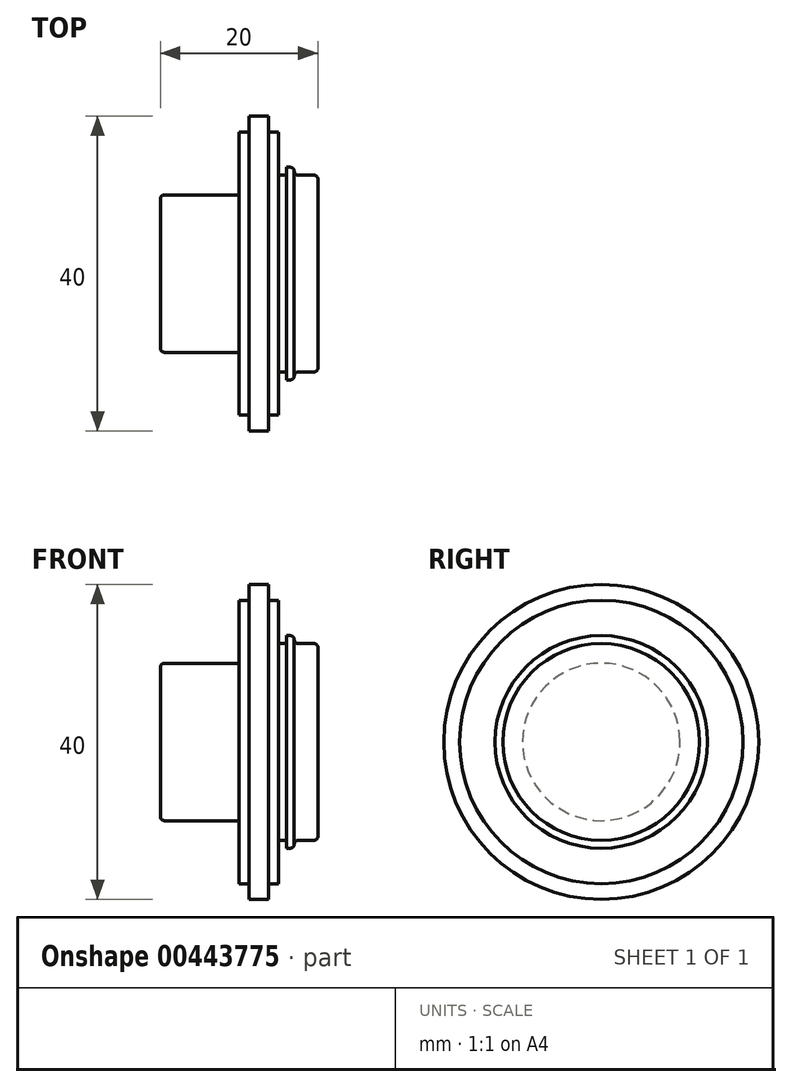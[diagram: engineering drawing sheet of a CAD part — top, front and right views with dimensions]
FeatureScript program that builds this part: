
annotation { "Feature Type Name" : "Feature", "Feature Type Description" : "" }
export const myFeature = defineFeature(function(context is Context, id is Id, definition is map)
    precondition{}
    {
        {
            var Q0;
            Q0=qCreatedBy(makeId("Front.planeOp"),FACE);
            var sketch = newSketch(context, id + "F0", { "sketchPlane" : qUnion([Q0])});
            skLineSegment(sketch, "E0", {"start": v(0, 0) * mm, "end": v(-20, 0) * mm});
            skLineSegment(sketch, "E1", {"start": v(-20, 0) * mm, "end": v(-20, 10) * mm});
            skLineSegment(sketch, "E2", {"start": v(-20, 10) * mm, "end": v(-10, 10) * mm});
            skLineSegment(sketch, "E3", {"start": v(-10, 10) * mm, "end": v(-10, 18) * mm});
            skLineSegment(sketch, "E4", {"start": v(-10, 18) * mm, "end": v(-8.75, 18) * mm});
            skLineSegment(sketch, "E5", {"start": v(-8.75, 18) * mm, "end": v(-8.75, 20) * mm});
            skLineSegment(sketch, "E6", {"start": v(-8.75, 20) * mm, "end": v(-6.25, 20) * mm});
            skLineSegment(sketch, "E7", {"start": v(-6.25, 20) * mm, "end": v(-6.25, 18) * mm});
            skLineSegment(sketch, "E8", {"start": v(-6.25, 18) * mm, "end": v(-5, 18) * mm});
            skLineSegment(sketch, "E9", {"start": v(-5, 18) * mm, "end": v(-5, 12.5) * mm});
            skLineSegment(sketch, "E10", {"start": v(-5, 12.5) * mm, "end": v(-4, 12.5) * mm});
            skLineSegment(sketch, "E11", {"start": v(-4, 12.5) * mm, "end": v(-4, 13.5) * mm});
            skLineSegment(sketch, "E12", {"start": v(-4, 13.5) * mm, "end": v(-3, 13.5) * mm});
            skLineSegment(sketch, "E13", {"start": v(-3, 13.5) * mm, "end": v(-3, 12.5) * mm});
            skLineSegment(sketch, "E14", {"start": v(-3, 12.5) * mm, "end": v(0, 12.5) * mm});
            skLineSegment(sketch, "E15", {"start": v(0, 12.5) * mm, "end": v(0, 0) * mm});
            skSolve(sketch);
        }
        {
            var Q0;
            Q0 = qSketchRegion(id + "F0", true);
            var Q1;
            Q1=sQuery(id+"F0.wireOp",EDGE,"E0");
            revolve(context, id + "F1", {"entities" : qUnion([Q0]), "axis" : qUnion([Q1]), "revolveType" : RevolveType.FULL});
        }
        {
            var Q0;
            Q0=makeQuery(id+"F1.opRevolve","SWEPT_EDGE",EDGE,{"disambiguationData":[OSD([sQuery(id+"F0.wireOp",EDGE,"E1"),sQuery(id+"F0.wireOp",EDGE,"E2")])]});
            var Q1;
            Q1=makeQuery(id+"F1.opRevolve","SWEPT_EDGE",EDGE,{"disambiguationData":[OSD([sQuery(id+"F0.wireOp",EDGE,"E12"),sQuery(id+"F0.wireOp",EDGE,"E13")])]});
            var Q2;
            Q2=makeQuery(id+"F1.opRevolve","SWEPT_FACE",FACE,{"disambiguationData":[OSD([sQuery(id+"F0.wireOp",EDGE,"E14")])]});
            fillet(context, id + "F2", {"entities" : qUnion([Q0, Q1, Q2]), "radius" : 0.5 * mm, "tangentPropagation" : true, "allowEdgeOverflow" : false});
        }
    });
